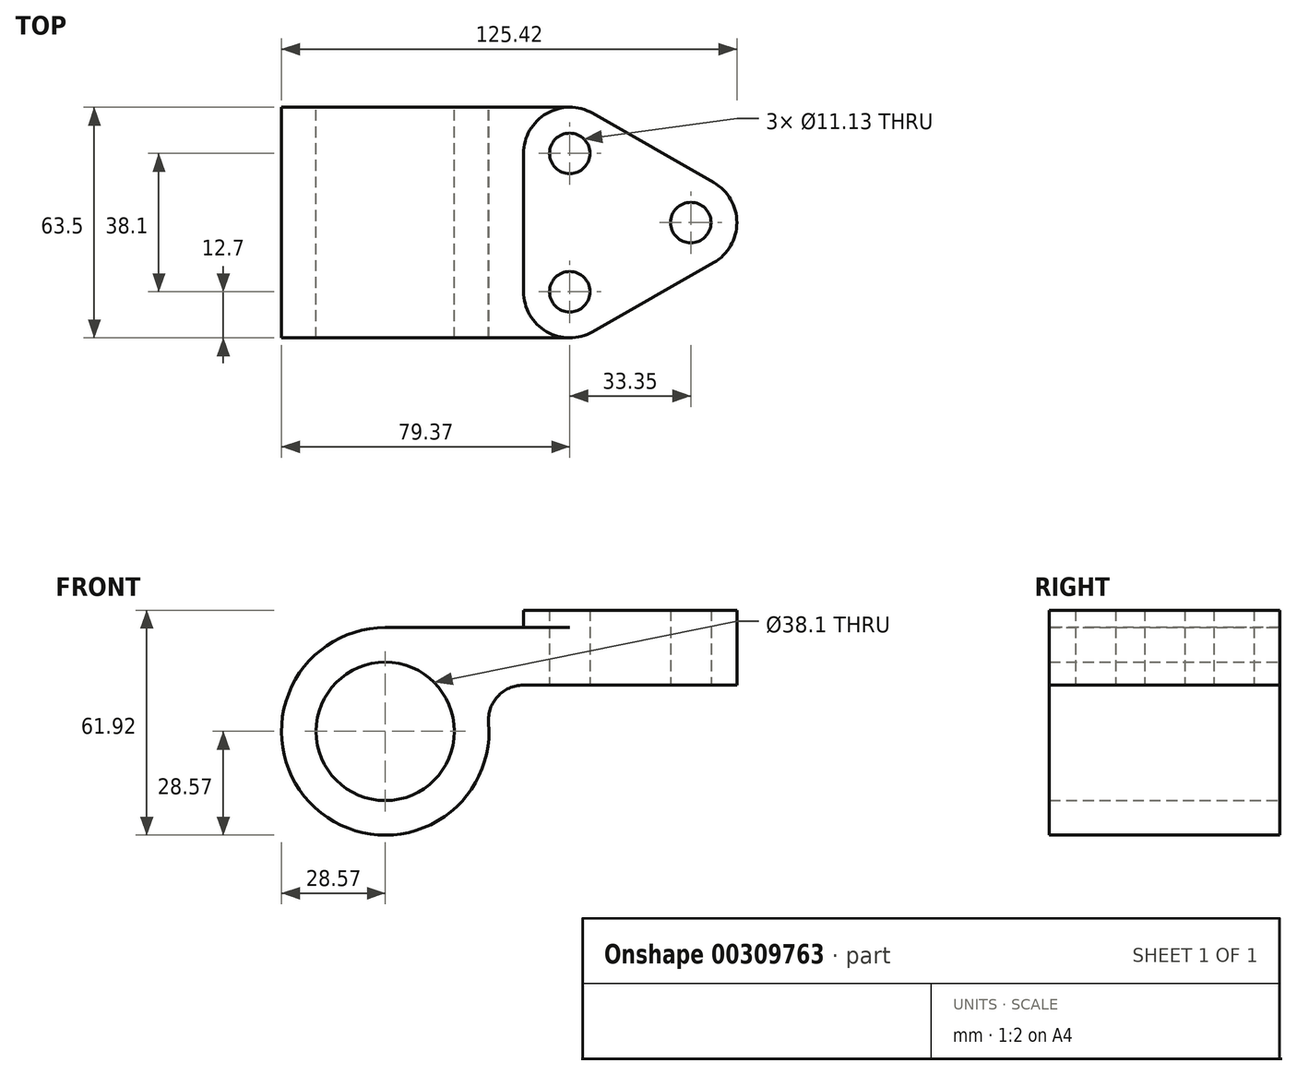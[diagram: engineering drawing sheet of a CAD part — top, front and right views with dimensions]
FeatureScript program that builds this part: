
annotation { "Feature Type Name" : "Feature", "Feature Type Description" : "" }
export const myFeature = defineFeature(function(context is Context, id is Id, definition is map)
    precondition{}
    {
        {
            var Q0;
            Q0=qCreatedBy(makeId("Front.planeOp"),FACE);
            var sketch = newSketch(context, id + "F0", { "sketchPlane" : qUnion([Q0])});
            skArc(sketch, "E0", {"start": v(0, 28.57) * mm, "mid": v(-19.35, -21.03) * mm, "end": v(28.48, 2.38) * mm});
            skCircle(sketch, "E1", {"center": v(0, 0) * mm, "radius": 19.05 * mm});
            skArc(sketch, "E2", {"start": v(28.48, 2.38) * mm, "mid": v(30.96, 9.62) * mm, "end": v(37.97, 12.7) * mm});
            skLineSegment(sketch, "E3", {"start": v(37.97, 12.7) * mm, "end": v(50.8, 12.7) * mm});
            skLineSegment(sketch, "E4", {"start": v(50.8, 12.7) * mm, "end": v(50.8, 28.58) * mm});
            skLineSegment(sketch, "E5", {"start": v(50.8, 28.57) * mm, "end": v(0, 28.57) * mm});
            skSolve(sketch);
        }
        {
            var Q0;
            Q0 = qSketchRegion(id + "F0", true);
            extrude(context, id + "F1", {"entities" : qUnion([Q0]), "endBound" : BoundingType.SYMMETRIC, "depth" : 63.5 * mm});
        }
        {
            var Q0;
            Q0=makeQuery(id+"F1.opExtrude","SWEPT_FACE",FACE,{"disambiguationData":[OSD([sQuery(id+"F0.wireOp",EDGE,"E5")])]});
            var sketch = newSketch(context, id + "F2", { "sketchPlane" : qUnion([Q0])});
            skPoint(sketch, "E6.endSnap0", {"position": v(50.8, 0) * mm});
            skLineSegment(sketch, "E7", {"start": v(0, 0) * mm, "end": v(98, 0) * mm, "construction": true});
            skCircle(sketch, "E8", {"center": v(50.8, 19.05) * mm, "radius": 5.56 * mm});
            skCircle(sketch, "E9.MirrorC", {"center": v(50.8, -19.05) * mm, "radius": 5.56 * mm});
            skCircle(sketch, "E10", {"center": v(84.15, 0) * mm, "radius": 5.56 * mm});
            skLineSegment(sketch, "E11", {"start": v(38.1, 19.05) * mm, "end": v(38.1, -19.05) * mm});
            skLineSegment(sketch, "E12", {"start": v(57.1, 30.08) * mm, "end": v(90.45, 11.03) * mm});
            skLineSegment(sketch, "E13", {"start": v(57.1, -30.08) * mm, "end": v(90.45, -11.03) * mm});
            skArc(sketch, "E14", {"start": v(90.45, 11.03) * mm, "mid": v(96.85, 0) * mm, "end": v(90.45, -11.03) * mm});
            skArc(sketch, "E15", {"start": v(38.1, 19.05) * mm, "mid": v(44.42, 30.03) * mm, "end": v(57.1, 30.08) * mm});
            skArc(sketch, "E16", {"start": v(38.1, -19.05) * mm, "mid": v(44.42, -30.03) * mm, "end": v(57.1, -30.08) * mm});
            skSolve(sketch);
        }
        {
            var Q0;
            Q0 = qSketchRegion(id + "F2", true);
            extrude(context, id + "F3", {"entities" : qUnion([Q0]), "operationType" : NewBodyOperationType.ADD, "depth" : 4.78 * mm});
        }
        {
            var Q0;
            {var subQ0=sQuery(id+"F2.wireOp",EDGE,"E8");Q0=makeQuery(id+"F3.boolean.opBoolean","SPLIT",FACE,{"disambiguationData":[TD([makeQuery(id+"F3.opExtrude","SWEPT_FACE",FACE,{"disambiguationData":[OSD([subQ0])]})])],"derivedFrom":makeQuery(id+"F1.opExtrude","SWEPT_FACE",FACE,{"disambiguationData":[OSD([sQuery(id+"F0.wireOp",EDGE,"E5")])]})});}
            var Q1;
            {var subQ0=sQuery(id+"F2.wireOp",EDGE,"E9.MirrorC");Q1=makeQuery(id+"F3.boolean.opBoolean","SPLIT",FACE,{"disambiguationData":[TD([makeQuery(id+"F3.opExtrude","SWEPT_FACE",FACE,{"disambiguationData":[OSD([subQ0])]})])],"derivedFrom":makeQuery(id+"F1.opExtrude","SWEPT_FACE",FACE,{"disambiguationData":[OSD([sQuery(id+"F0.wireOp",EDGE,"E5")])]})});}
            extrude(context, id + "F4", {"entities" : qUnion([Q0, Q1]), "operationType" : NewBodyOperationType.REMOVE, "endBound" : BoundingType.THROUGH_ALL, "oppositeDirection" : true, "depth" : 25.4 * mm});
        }
        {
            var Q0;
            Q0=makeQuery(id+"F3.opExtrude","CAP_FACE",FACE,{"disambiguationData":[OSD([sQuery(id+"F2.wireOp",EDGE,"E8"),sQuery(id+"F2.wireOp",EDGE,"E9.MirrorC"),sQuery(id+"F2.wireOp",EDGE,"E10"),sQuery(id+"F2.wireOp",EDGE,"E11"),sQuery(id+"F2.wireOp",EDGE,"E12"),sQuery(id+"F2.wireOp",EDGE,"E13"),sQuery(id+"F2.wireOp",EDGE,"E14"),sQuery(id+"F2.wireOp",EDGE,"E15"),sQuery(id+"F2.wireOp",EDGE,"E16")])],"isStart":true});
            extrude(context, id + "F5", {"entities" : qUnion([Q0]), "operationType" : NewBodyOperationType.ADD, "depth" : 15.88 * mm});
        }
    });
